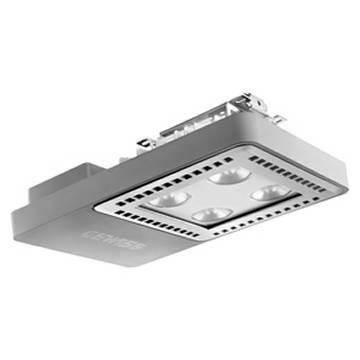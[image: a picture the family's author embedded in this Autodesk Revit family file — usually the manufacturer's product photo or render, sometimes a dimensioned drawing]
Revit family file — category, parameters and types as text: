
# Revit family: Lighting-Industriale-GEWISS-SMART[4]HE_APPARECCHI-LED_1M_DALI
name_source: partatom
category: Apparecchi per illuminazione
units: mm (PartAtom-declared; Revit-internal decimal feet)

## family parameters
Basato su piano di lavoro = Sì
Condiviso = No
Numero OmniClass = 23.80.00.00
Punto di calcolo locali = Sì
Quota connettore circolare = Usa diametro
Sempre verticale = No
Sorgente d'illuminazione = No
Taglio con vuoti quando caricato = No
Tipo di parte = Normale
Titolo OmniClass = Electric Power and Lighting

## types (1)
- Lighting-Industriale-GEWISS-SMART[4]HE_APPARECCHI-LED_1M_DALI
    Alimentatore = Incluso
    Apparecchio a ridotta temperatura superficiale = Si
    Applicazione = Interno
    Cablaggio = Con connettore stagno Gw connect
    Caratteristiche elettriche e gestione della luce = -
    Caratteristiche ottiche e illuminotecniche = -
    Carico apparente = 50 VA
    Catalogo = LIGHTING
    Certificazione DIN 18032-3 = Con Staffa - Kit Funi + morsetto (in approvazione)
    Certificazioni e classificazioni = -
    Classe fotobiologica = RG0
    Classe isolamento = I
    Classificazione = Lighting
    Classificazione: = -
    Codice Electrocod = 2444
    Codice digitale univoco (Datamatrix) = Datamatrix
    Colore = Grigio RAL 7035
    Commenti sul wattaggio = 50W
    Contesto = Illuminazione di logistiche e locali produttivi industriali
    Controllo abbagliamento e luminanza = -
    Corpo = PA6 “Halogen Free” caricato fibra vetro
    Descrizione = SMART[4]LB 1M C.PAS.DALI ELL.57K
    Dispositivo di protezione = DM 6 kV / CM 10 kV
    Distanza tot_plafoniera = 74 mm  [stored 0.242782 ft]
    Durata di vita = L90B10 (Tq+25°C) = 100.000 h - L90B10 (Tq+50°C) = 50.000 h
    Efficienza luminosa (lm/W) = 131
    Finitura colore = Grigio RAL 7035
    Fissaggio = -
    Frequenza nominale (Hz) = 50/60 Hz
    Gancio di chiusura = -
    Garanzia = 5 anni
    Grado di protezione = IP66
    Gruppo ottico = Riflettore in PC metallizzato e lenti in PMMA
    Guarnizioni = tipo siliconico antinvecchiamento
    IDF = 35c11ef9-9684-4acc-8d12-75d744717c91
    IDT = 9d21ab41a4404c819d8f88b838f402fb
    IPEA = -
    Immagine tipo = GWL1071.jpg
    Inclinazione = Con accessorio staffa
    Indice di resa cromatica = CRI-80
    Informazioni generali = -
    Installazione e manutenzione = -
    Lampada = LED
    Larghezza = 253 mm  [stored 0.830052 ft]
    Lumen output (lm) = 6300
    Lunghezza = 383 mm  [stored 1.25656 ft]
    Materiali = -
    Modello = GWS4123AQ857
    Motore = <Per categoria>
    Norma di riferimento = EN 60598-1 ; EN 60598-2-1 ; EN 60598-2-24
    Ottica = Ellittica
    Peso (kg): = 3,5
    Plafoniera = <Per categoria>
    Potenza di sistema = 48W
    Produttore = GEWISS S.p.A.
    Prospetto di default = 1219 mm
    Raggio led = 30 mm  [stored 0.0984252 ft]
    Resistenza agli urti = IK08
    Resistenza al filo incandescente = 850 °C
    SEO = Low Bay
    Scheda Tecnica = https://www.gewiss.com
    Schermo = Vetro Temprato Spessore 4mm
    Sistema di controllo = 1 x DALI DT6
    Sistema di controllo : = DALI
    Sostituibilità gruppo ottico = Non sostituibile
    Sostituibilità piastra di cablaggio = Non sostituibile
    Spessore plafoniera = 40 mm  [stored 0.131234 ft]
    Superficie massima esposta al vento : = 0,097 m²
    Temperatura di colore = 5700K
    Temperatura di esercizio = -30°C ÷ +50 °C
    Temperatura di stoccaggio = -40 +70 °C
    Tensione di alimentazione = 220 - 240 V
    Tipo di apparecchio = Riflettore industriale a LED&nbsp;
    Tipo di installazione e montaggio = Plafone - Parete - Sospensione
    Tipologia sorgente luminosa = LED - Non sostituibile
    Tolleranza cromatica = SDCM = 3
    Trasformatore = <Per categoria>
    URL = https://www.gewiss.com
    Vano di alimentazione = Integrato
    Versione file RFA = 20.11
    Vetro acceso = Lampada accesa
    Viti esterne = Acciaio inox
    Voltaggio = 230 V

note: [stored X ft] marks values corroborated as IEEE doubles in the binary element streams (Revit-internal decimal feet)

## geometry (parser evidence)
native form markers: Blend x4
no freeform markers — native parametric forms only
